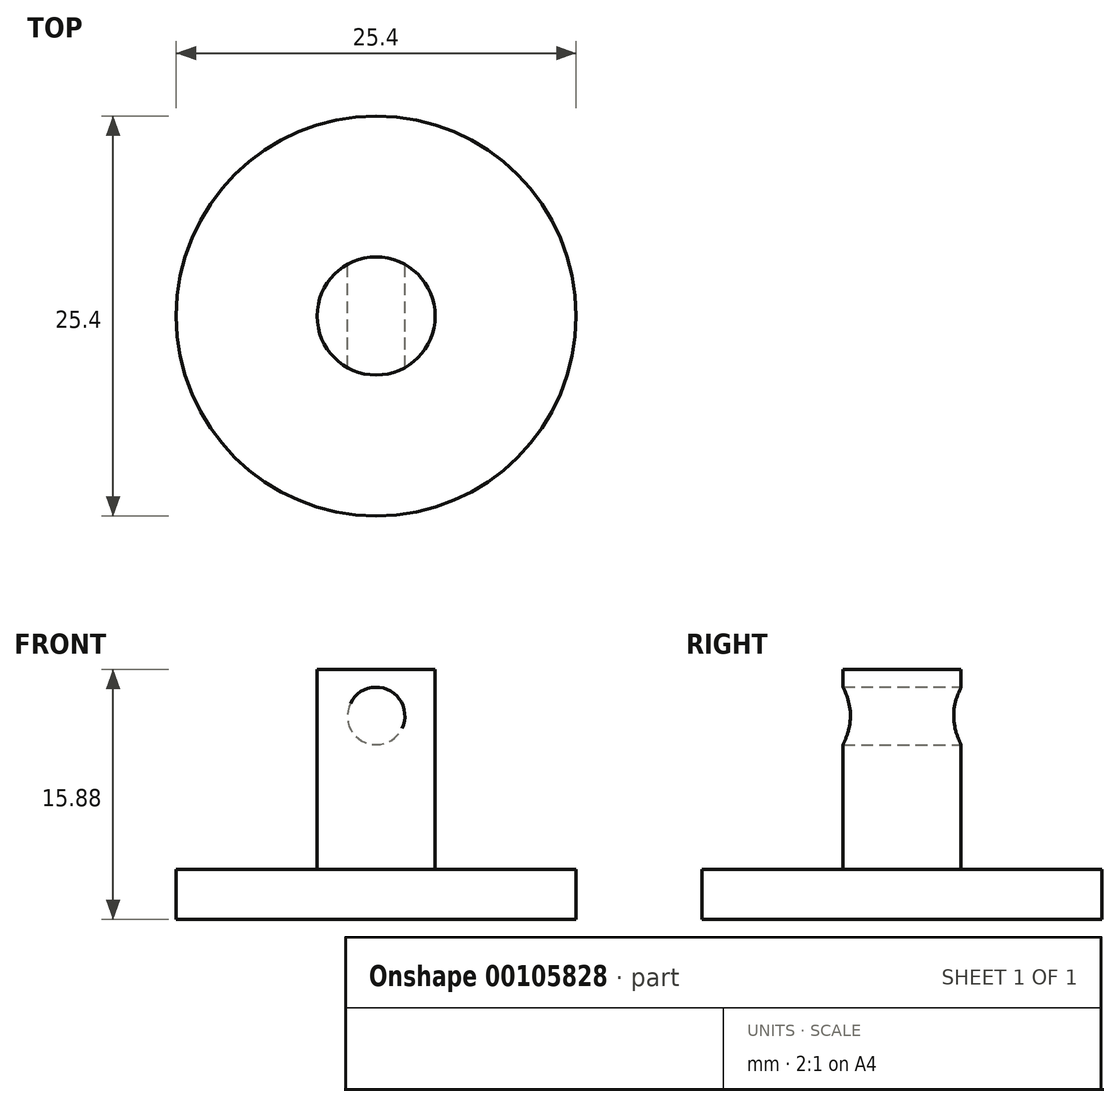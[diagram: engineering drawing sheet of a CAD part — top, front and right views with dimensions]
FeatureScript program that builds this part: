
annotation { "Feature Type Name" : "Feature", "Feature Type Description" : "" }
export const myFeature = defineFeature(function(context is Context, id is Id, definition is map)
    precondition{}
    {
        {
            var Q0;
            Q0=qCreatedBy(makeId("Top.planeOp"),FACE);
            var sketch = newSketch(context, id + "F0", { "sketchPlane" : qUnion([Q0])});
            skCircle(sketch, "E0", {"center": v(0, 0) * mm, "radius": 12.7 * mm});
            skSolve(sketch);
        }
        {
            var Q0;
            Q0=qSketchRegion(id+"F0",true);
            extrude(context, id + "F1", {"entities" : qUnion([Q0]), "depth" : 3.17 * mm});
        }
        {
            var Q0;
            Q0=makeQuery(id+"F1.opExtrude","CAP_FACE",FACE,{"disambiguationData":[OSD([sQuery(id+"F0.wireOp",EDGE,"E0")])],"isStart":false});
            var sketch = newSketch(context, id + "F2", { "sketchPlane" : qUnion([Q0])});
            skCircle(sketch, "E1", {"center": v(0, 0) * mm, "radius": 3.75 * mm});
            skSolve(sketch);
        }
        {
            var Q0;
            Q0=qSketchRegion(id+"F2",true);
            extrude(context, id + "F3", {"entities" : qUnion([Q0]), "operationType" : NewBodyOperationType.ADD, "depth" : 12.7 * mm});
        }
        {
            var Q0;
            Q0=qCreatedBy(makeId("Front.planeOp"),FACE);
            var sketch = newSketch(context, id + "F4", { "sketchPlane" : qUnion([Q0])});
            skCircle(sketch, "E2", {"center": v(0, 12.93) * mm, "radius": 1.83 * mm});
            skCircle(sketch, "E3", {"center": v(0, 12.92) * mm, "radius": 1.83 * mm});
            skSolve(sketch);
        }
        {
            var Q0;
            Q0 = qSketchRegion(id + "F4", true);
            var Q1;
            Q1=sQuery(id+"F4.wireOp",EDGE,"E2");
            extrude(context, id + "F5", {"entities" : qUnion([Q0]), "operationType" : NewBodyOperationType.REMOVE, "surfaceEntities" : qUnion([Q1]), "depth" : 5.08 * mm});
        }
        {
            var Q0;
            Q0 = qSketchRegion(id + "F4", true);
            extrude(context, id + "F6", {"entities" : qUnion([Q0]), "operationType" : NewBodyOperationType.REMOVE, "oppositeDirection" : true, "depth" : 25.4 * mm});
        }
    });
